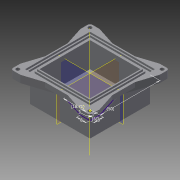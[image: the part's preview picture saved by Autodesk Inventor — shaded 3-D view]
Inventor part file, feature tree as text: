
AUTODESK INVENTOR PART (.ipt)
format: ipt  version: 2015 (Build 190159000, 159)  size: 354,816 bytes
history: native  units: in
note: dims shown in document units (in); Inventor stores cm internally (conversion verified against a paired STEP export)
features: sketch x9, extrude x7, projected_geometry x7, plane x3, hole x2, fillet x2, mirror x2, other x1, rib x1
ambient origin geometry x8: Origin, YZ Plane, XZ Plane, XY Plane, X Axis, Y Axis, Z Axis, Center Point
bodies: Solid1 (feature_tree)
feature tree (34):
  extrude  "Extrusion1"  Depth=1.9685in
  extrude  "Extrusion2"  Depth=0.0394in
  extrude  "Extrusion3"  Depth=0.0394in
  extrude  "Extrusion4"  Depth=0.0394in
  extrude  "Extrusion6"  Depth=0.0394in TaperAngle=0.0deg
  extrude  "Extrusion5"  Depth=0.0394in
  hole  "Hole1"  [1 undecoded]
  fillet  "Fillet1"  Radius=0.315in
  extrude  "Extrusion7"  Depth=0.2362in
  fillet  "Fillet2"  Radius=1.9685in
  sketch  "Sketch12"  dims[d22=0.1181in d23=0.2362in d24=0.1575in d25=0.0787in d26=90.0deg d27=0.315in d28=0.8108in d29=1.9685in d30=0.0787in d31=0.1181in d32=0.0394in d33=0.1181in d34=0.2362in d35=0.1181in d36=0.1181in d37=45.0deg d38=135.0deg d39=0.0394in d40=0.0787in d41=0.0in d42=0.0in d43=0.0394in d44=0.0394in d45=-0.9843in d46=-0.9843in d47=0.7382in d50=0.0394in d51=0.0394in d52=0.1181in d53=0.0394in d54=0.0in d55=0.0in d56=0.2362in d57=0.2362in d58=0.1575in d59=0.0in d60=0.0787in d61=0.1181in d62=0.1181in d63=0.2362in d64=0.1575in d65=0.0787in d66=90.0deg d67=0.315in d68=0.8108in]
  other  "Work Point1"
  hole  "Hole2"  [1 undecoded]
  plane  "Work Plane1"
  rib  "Rib1"
  plane  "Work Plane2"
  plane  "Work Plane3"
  mirror  "Mirror1"
  mirror  "Mirror3"
  sketch  "Sketch1"  dims[d0=1.9685in d1=1.9685in]
  sketch  "Sketch2"  dims[d2=0.0394in d3=0.0in d4=0.0394in]
  projected_geometry  "Projected Loop1"
  sketch  "Sketch3"  dims[d5=0.7874in d6=0.0in d7=0.0394in]
  projected_geometry  "Projected Loop2"
  sketch  "Sketch4"  dims[d8=0.0394in d9=0.0394in]
  projected_geometry  "Projected Loop3"
  sketch  "Sketch5"  dims[d10=0.0394in d11=0.0394in d12=0.0in]
  projected_geometry  "Projected Loop4"
  sketch  "Sketch8"  dims[d13=0.0394in d14=0.0394in]
  sketch  "Sketch10"  dims[d15=0.0591in d16=0.0in d17=0.315in d18=0.315in]
  projected_geometry  "Projected Loop5"
  projected_geometry  "Projected Loop6"
  projected_geometry  "Projected Loop7"
  sketch  "Sketch11"  dims[d19=0.0787in d20=0.0in d21=0.2362in]
note: 2 required parameter values undecoded (feature->parameter linkage not recoverable at this tier; creation-order binding heuristic only, values carry confidence <= 0.55)
